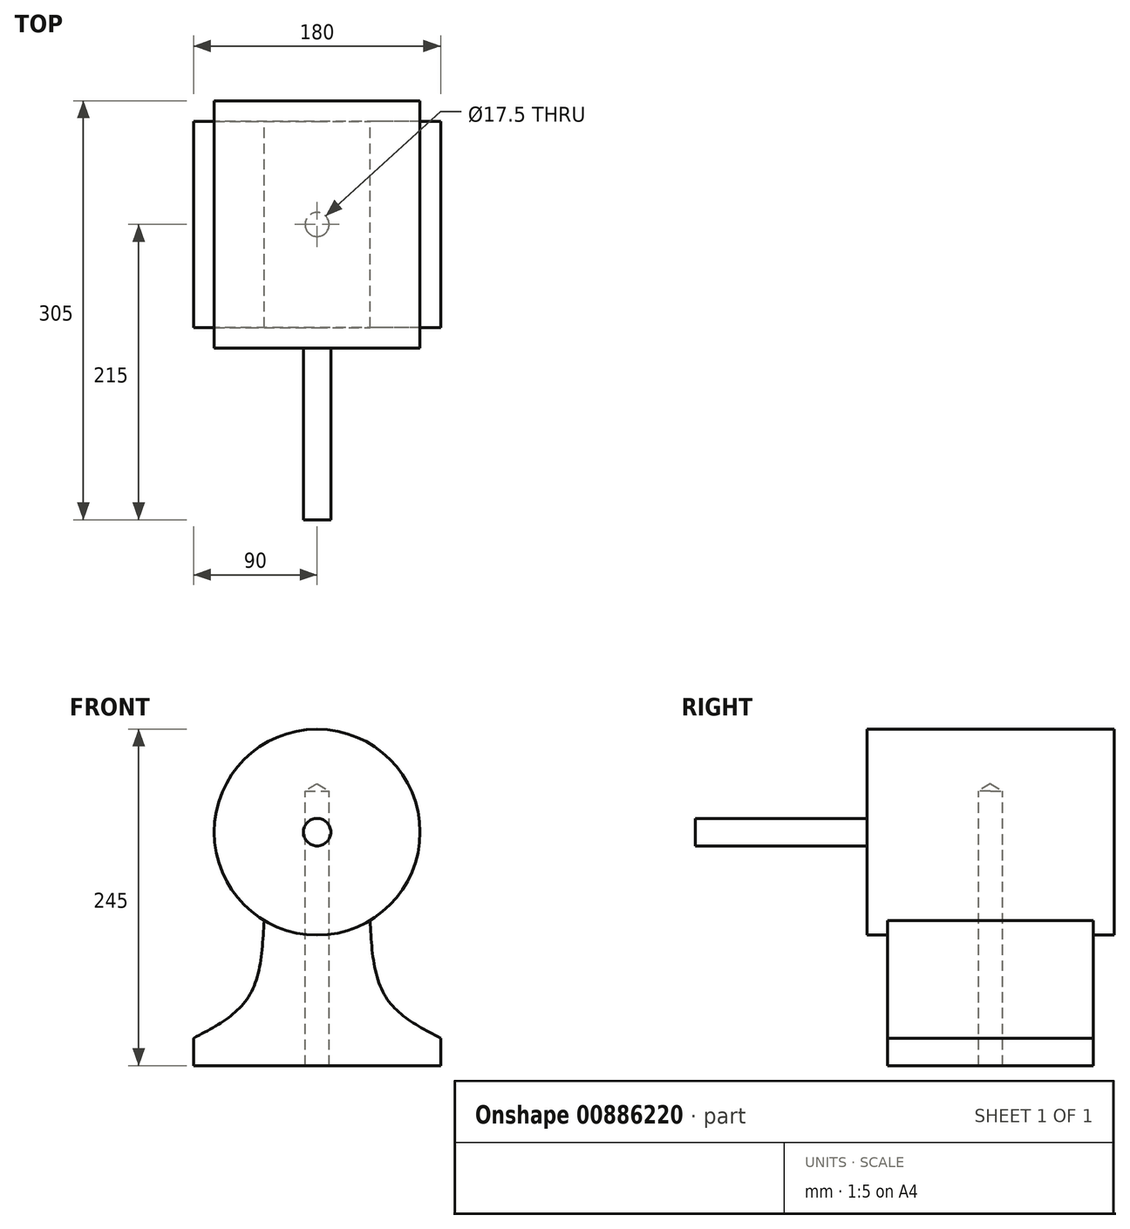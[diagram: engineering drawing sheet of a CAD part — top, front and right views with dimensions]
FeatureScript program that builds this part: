
annotation { "Feature Type Name" : "Feature", "Feature Type Description" : "" }
export const myFeature = defineFeature(function(context is Context, id is Id, definition is map)
    precondition{}
    {
        {
            var Q0;
            Q0=qCreatedBy(makeId("Front.planeOp"),FACE);
            var sketch = newSketch(context, id + "F0", { "sketchPlane" : qUnion([Q0])});
            skLineSegment(sketch, "E0.bottom", {"start": v(90, -10) * mm, "end": v(-90, -10) * mm});
            skLineSegment(sketch, "E0.top", {"start": v(90, 10) * mm, "end": v(-90, 10) * mm});
            skLineSegment(sketch, "E0.left", {"start": v(90, -10) * mm, "end": v(90, 10) * mm});
            skLineSegment(sketch, "E0.right", {"start": v(-90, -10) * mm, "end": v(-90, 10) * mm});
            skPoint(sketch, "E0.middle", {"position": v(0, 0) * mm});
            skCircle(sketch, "E1", {"center": v(0, 160) * mm, "radius": 75 * mm});
            skLineSegment(sketch, "E2", {"start": v(0, 10) * mm, "end": v(50, 10) * mm});
            skLineSegment(sketch, "E3", {"start": v(50, 10) * mm, "end": v(50, 40) * mm});
            skFitSpline(sketch, "E4", {"points": [v(90, 10) * mm, v(50, 40) * mm, v(38.59, 95.69) * mm], "startDerivative": vector(-97.3, 50.87) * mm, "endDerivative": vector(-6.5, 119.77) * mm});
            skLineSegment(sketch, "E5", {"start": v(-90, 10) * mm, "end": v(-50, 10) * mm});
            skLineSegment(sketch, "E6", {"start": v(-50, 10) * mm, "end": v(-50, 40) * mm});
            skFitSpline(sketch, "E7", {"points": [v(-90, 10) * mm, v(-50, 40) * mm, v(-38.59, 95.69) * mm], "startDerivative": vector(97.3, 50.87) * mm, "endDerivative": vector(6.5, 119.77) * mm});
            skSolve(sketch);
        }
        {
            var Q0;
            {var subQ0=sQuery(id+"F0.wireOp",EDGE,"E1");var subQ1=makeQuery(id+"F0.imprint","INTERSECT",VERTEX,{"derivedFrom":[subQ0,sQuery(id+"F0.wireOp",EDGE,"E4")]});Q0=makeQuery(id+"F0.imprint","IMPRINT",FACE,{"disambiguationData":[TD([[makeQuery(id+"F0.imprint","IMPRINT",EDGE,{"disambiguationData":[TD([[subQ1,1.0]])],"derivedFrom":subQ0}),1.0]])]});}
            extrude(context, id + "F1", {"entities" : qUnion([Q0]), "depth" : 180 * mm, "offsetDistance" : 25 * mm, "symmetric" : true});
        }
        {
            var Q0;
            Q0 = qSketchRegion(id + "F0", true);
            extrude(context, id + "F2", {"entities" : qUnion([Q0]), "operationType" : NewBodyOperationType.ADD, "depth" : 150 * mm, "offsetDistance" : 25 * mm, "symmetric" : true});
        }
        {
            var Q0;
            Q0=makeQuery(id+"F1.opExtrude","CAP_FACE",FACE,{"disambiguationData":[OSD([sQuery(id+"F0.wireOp",EDGE,"E1")])],"isStart":false});
            var sketch = newSketch(context, id + "F3", { "sketchPlane" : qUnion([Q0])});
            skCircle(sketch, "E8", {"center": v(0, 160) * mm, "radius": 10 * mm});
            skSolve(sketch);
        }
        {
            var Q0;
            Q0 = qSketchRegion(id + "F3", true);
            extrude(context, id + "F4", {"entities" : qUnion([Q0]), "operationType" : NewBodyOperationType.ADD, "depth" : 125 * mm, "offsetDistance" : 25 * mm});
        }
        {
            var Q0;
            Q0=makeQuery(id+"F2.opExtrude","SWEPT_FACE",FACE,{"disambiguationData":[OSD([sQuery(id+"F0.wireOp",EDGE,"E0.bottom")])]});
            var sketch = newSketch(context, id + "F5", { "sketchPlane" : qUnion([Q0])});
            skCircle(sketch, "E9", {"center": v(0, 0) * mm, "radius": 8 * mm});
            skSolve(sketch);
        }
        {
            var Q0;
            Q0=sQuery(id+"F5.wireOp",VERTEX,"E9.center");
            var Q1;
            Q1=makeQuery(id+"F1.opExtrude","SWEPT_BODY",BODY,{"disambiguationData":[OSD([sQuery(id+"F0.wireOp",EDGE,"E1")])]});
            hole(context, id + "F6", {"style" : HoleStyle.SIMPLE, "endStyle" : HoleEndStyle.BLIND, "standardTappedOrClearance" : lookupTablePath({ "fit" : "Normal", "standard" : "ISO", "size" : "M16", "type" : "Clearance" }), "standardBlindInLast" : lookupTablePath({ "fit" : "Normal", "standard" : "ISO", "size" : "M16", "type" : "Clearance" }), "holeDiameter" : 17.5 * mm, "majorDiameter" : 5 * mm, "holeDepth" : 200 * mm, "isTappedThrough" : true, "tappedDepth" : 995.5 * mm, "tapClearance" : 3, "locations" : qUnion([Q0]), "scope" : qUnion([Q1])});
        }
    });
